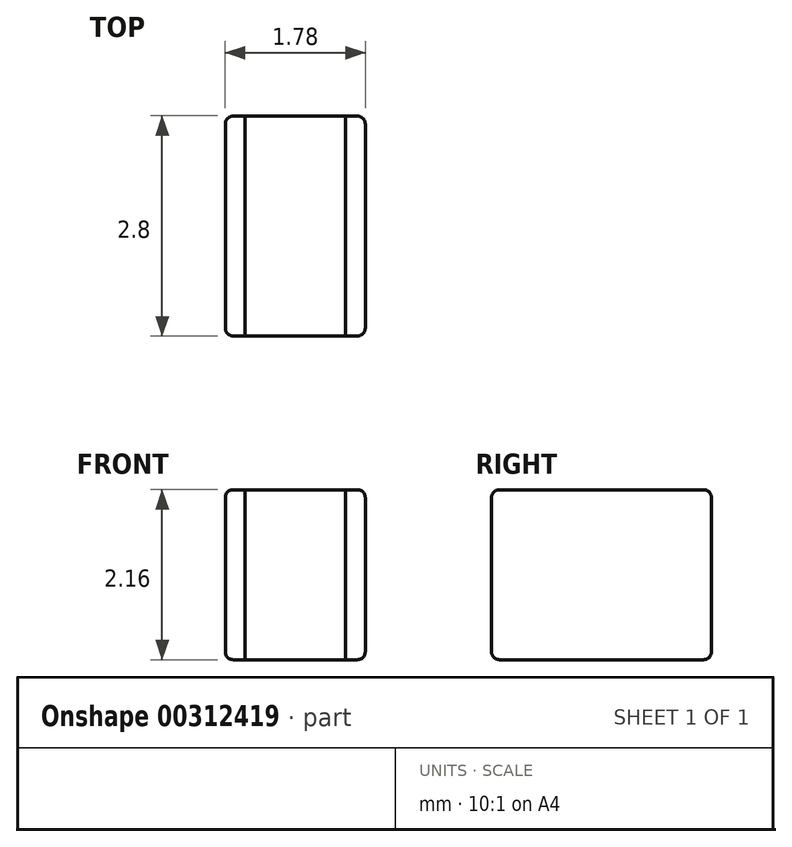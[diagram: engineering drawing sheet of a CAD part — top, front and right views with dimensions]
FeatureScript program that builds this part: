
annotation { "Feature Type Name" : "Feature", "Feature Type Description" : "" }
export const myFeature = defineFeature(function(context is Context, id is Id, definition is map)
    precondition{}
    {
        {
            assignVariable(context, id + "F0", {"name" : "T", "anyValue" : 2.16 * mm});
        }
        {
            assignVariable(context, id + "F1", {"name" : "r", "anyValue" : 0.1});
        }
        {
            var Q0;
            Q0=qCreatedBy(makeId("Top.planeOp"),FACE);
            var sketch = newSketch(context, id + "F2", { "sketchPlane" : qUnion([Q0])});
            skLineSegment(sketch, "E0.bottom", {"start": v(0.64, 1.4) * mm, "end": v(-0.64, 1.4) * mm});
            skLineSegment(sketch, "E0.top", {"start": v(0.64, -1.4) * mm, "end": v(-0.64, -1.4) * mm});
            skLineSegment(sketch, "E0.left", {"start": v(0.64, 1.4) * mm, "end": v(0.64, -1.4) * mm});
            skLineSegment(sketch, "E0.right", {"start": v(-0.64, 1.4) * mm, "end": v(-0.64, -1.4) * mm});
            skPoint(sketch, "E0.middle", {"position": v(0, 0) * mm});
            skLineSegment(sketch, "E1", {"start": v(0.64, 1.4) * mm, "end": v(0.89, 1.4) * mm});
            skLineSegment(sketch, "E2", {"start": v(0.89, 1.4) * mm, "end": v(0.89, -1.4) * mm});
            skLineSegment(sketch, "E3", {"start": v(0.89, -1.4) * mm, "end": v(0.64, -1.4) * mm});
            skLineSegment(sketch, "E4", {"start": v(-0.64, -1.4) * mm, "end": v(-0.89, -1.4) * mm});
            skLineSegment(sketch, "E5", {"start": v(-0.89, -1.4) * mm, "end": v(-0.89, 1.4) * mm});
            skLineSegment(sketch, "E6", {"start": v(-0.89, 1.4) * mm, "end": v(-0.64, 1.4) * mm});
            skSolve(sketch);
        }
        {
            var Q0;
            Q0=makeQuery(id+"F2.imprint","IMPRINT",FACE,{"disambiguationData":[TD([[makeQuery(id+"F2.imprint","IMPRINT",EDGE,{"derivedFrom":sQuery(id+"F2.wireOp",EDGE,"E0.bottom")}),1.0]])]});
            extrude(context, id + "F3", {"entities" : qUnion([Q0]), "endBound" : BoundingType.SYMMETRIC, "depth" : (getVariable(context, 'T'))});
        }
        {
            var Q0;
            Q0=makeQuery(id+"F2.imprint","IMPRINT",FACE,{"disambiguationData":[TD([[makeQuery(id+"F2.imprint","IMPRINT",EDGE,{"derivedFrom":sQuery(id+"F2.wireOp",EDGE,"E0.right")}),-1.0]])]});
            extrude(context, id + "F4", {"entities" : qUnion([Q0]), "endBound" : BoundingType.SYMMETRIC, "depth" : (getVariable(context, 'T'))});
        }
        {
            var Q0;
            Q0=makeQuery(id+"F2.imprint","IMPRINT",FACE,{"disambiguationData":[TD([[makeQuery(id+"F2.imprint","IMPRINT",EDGE,{"derivedFrom":sQuery(id+"F2.wireOp",EDGE,"E0.left")}),1.0]])]});
            extrude(context, id + "F5", {"entities" : qUnion([Q0]), "endBound" : BoundingType.SYMMETRIC, "depth" : (getVariable(context, 'T'))});
        }
        {
            var Q0;
            Q0=makeQuery(id+"F4.opExtrude","CAP_EDGE",EDGE,{"disambiguationData":[OSD([sQuery(id+"F2.wireOp",EDGE,"E4")])],"isStart":false});
            var Q1;
            Q1=makeQuery(id+"F3.opExtrude","CAP_EDGE",EDGE,{"disambiguationData":[OSD([sQuery(id+"F2.wireOp",EDGE,"E0.top")])],"isStart":false});
            var Q2;
            Q2=makeQuery(id+"F5.opExtrude","CAP_EDGE",EDGE,{"disambiguationData":[OSD([sQuery(id+"F2.wireOp",EDGE,"E3")])],"isStart":false});
            var Q3;
            Q3=makeQuery(id+"F5.opExtrude","SWEPT_FACE",FACE,{"disambiguationData":[OSD([sQuery(id+"F2.wireOp",EDGE,"E2")])]});
            var Q4;
            Q4=makeQuery(id+"F5.opExtrude","CAP_EDGE",EDGE,{"disambiguationData":[OSD([sQuery(id+"F2.wireOp",EDGE,"E3")])],"isStart":true});
            var Q5;
            Q5=makeQuery(id+"F3.opExtrude","CAP_EDGE",EDGE,{"disambiguationData":[OSD([sQuery(id+"F2.wireOp",EDGE,"E0.top")])],"isStart":true});
            var Q6;
            Q6=makeQuery(id+"F4.opExtrude","CAP_EDGE",EDGE,{"disambiguationData":[OSD([sQuery(id+"F2.wireOp",EDGE,"E4")])],"isStart":true});
            var Q7;
            Q7=makeQuery(id+"F3.opExtrude","CAP_EDGE",EDGE,{"disambiguationData":[OSD([sQuery(id+"F2.wireOp",EDGE,"E0.bottom")])],"isStart":false});
            var Q8;
            Q8=makeQuery(id+"F5.opExtrude","CAP_EDGE",EDGE,{"disambiguationData":[OSD([sQuery(id+"F2.wireOp",EDGE,"E1")])],"isStart":false});
            var Q9;
            Q9=makeQuery(id+"F5.opExtrude","CAP_EDGE",EDGE,{"disambiguationData":[OSD([sQuery(id+"F2.wireOp",EDGE,"E1")])],"isStart":true});
            var Q10;
            Q10=makeQuery(id+"F4.opExtrude","SWEPT_FACE",FACE,{"disambiguationData":[OSD([sQuery(id+"F2.wireOp",EDGE,"E5")])]});
            var Q11;
            Q11=makeQuery(id+"F4.opExtrude","CAP_EDGE",EDGE,{"disambiguationData":[OSD([sQuery(id+"F2.wireOp",EDGE,"E6")])],"isStart":true});
            var Q12;
            Q12=makeQuery(id+"F3.opExtrude","CAP_EDGE",EDGE,{"disambiguationData":[OSD([sQuery(id+"F2.wireOp",EDGE,"E0.bottom")])],"isStart":true});
            var Q13;
            Q13=makeQuery(id+"F4.opExtrude","CAP_EDGE",EDGE,{"disambiguationData":[OSD([sQuery(id+"F2.wireOp",EDGE,"E6")])],"isStart":false});
            fillet(context, id + "F6", {"entities" : qUnion([Q0, Q1, Q2, Q3, Q4, Q5, Q6, Q7, Q8, Q9, Q10, Q11, Q12, Q13]), "radius" : (getVariable(context, 'r')) * mm, "tangentPropagation" : true, "allowEdgeOverflow" : false});
        }
    });
